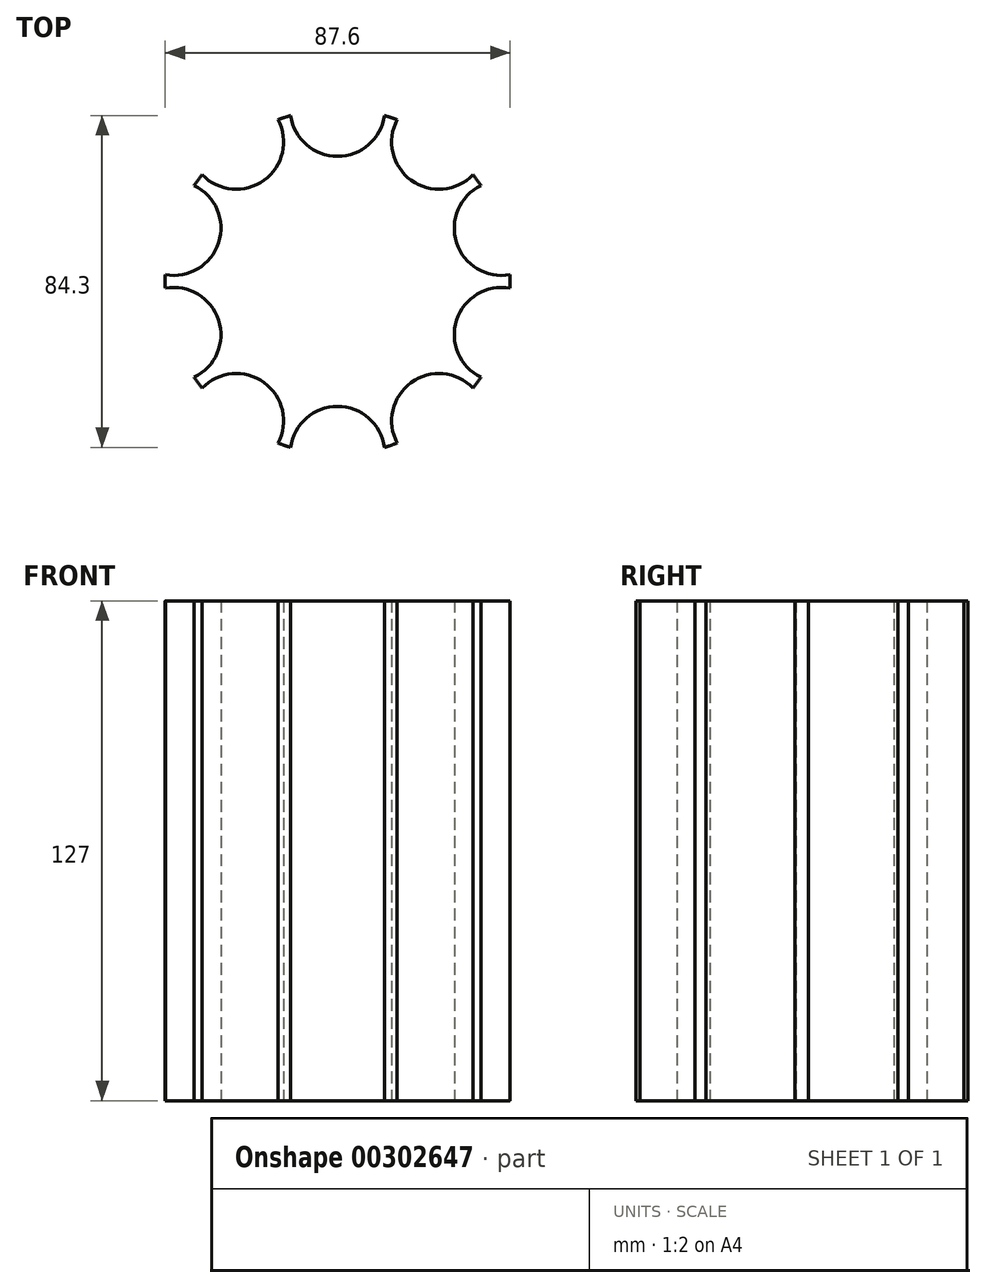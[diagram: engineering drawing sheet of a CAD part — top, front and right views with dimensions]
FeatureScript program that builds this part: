
annotation { "Feature Type Name" : "Feature", "Feature Type Description" : "" }
export const myFeature = defineFeature(function(context is Context, id is Id, definition is map)
    precondition{}
    {
        {
            var Q0;
            Q0=qCreatedBy(makeId("Top.planeOp"),FACE);
            var sketch = newSketch(context, id + "F0", { "sketchPlane" : qUnion([Q0])});
            skCircle(sketch, "E0", {"center": v(0, 0) * mm, "radius": 43.8 * mm});
            skCircle(sketch, "E1", {"center": v(0, 43.8) * mm, "radius": 12.02 * mm});
            skCircle(sketch, "E2.1.0", {"center": v(-25.75, 35.44) * mm, "radius": 12.02 * mm});
            skCircle(sketch, "E2.2.0", {"center": v(-41.66, 13.54) * mm, "radius": 12.02 * mm});
            skCircle(sketch, "E2.3.0", {"center": v(-41.66, -13.54) * mm, "radius": 12.02 * mm});
            skCircle(sketch, "E2.4.0", {"center": v(-25.75, -35.44) * mm, "radius": 12.02 * mm});
            skCircle(sketch, "E2.5.0", {"center": v(0, -43.8) * mm, "radius": 12.02 * mm});
            skCircle(sketch, "E2.6.0", {"center": v(25.75, -35.44) * mm, "radius": 12.02 * mm});
            skCircle(sketch, "E2.7.0", {"center": v(41.66, -13.54) * mm, "radius": 12.02 * mm});
            skCircle(sketch, "E2.8.0", {"center": v(41.66, 13.54) * mm, "radius": 12.02 * mm});
            skCircle(sketch, "E2.9.0", {"center": v(25.75, 35.44) * mm, "radius": 12.02 * mm});
            skSolve(sketch);
        }
        {
            var Q0;
            {var subQ0=sQuery(id+"F0.wireOp",EDGE,"E2.8.0");var subQ1=sQuery(id+"F0.wireOp",EDGE,"E0");var subQ17=makeQuery(id+"F0.imprint","INTERSECT",VERTEX,{"disambiguationData":[OD(0.0)],"derivedFrom":[subQ1,subQ0]});Q0=makeQuery(id+"F0.imprint","IMPRINT",FACE,{"disambiguationData":[TD([[makeQuery(id+"F0.imprint","IMPRINT",EDGE,{"disambiguationData":[TD([[subQ17,-1.0]])],"derivedFrom":subQ1}),1.0]])]});}
            extrude(context, id + "F1", {"entities" : qUnion([Q0]), "depth" : 127 * mm});
        }
    });
